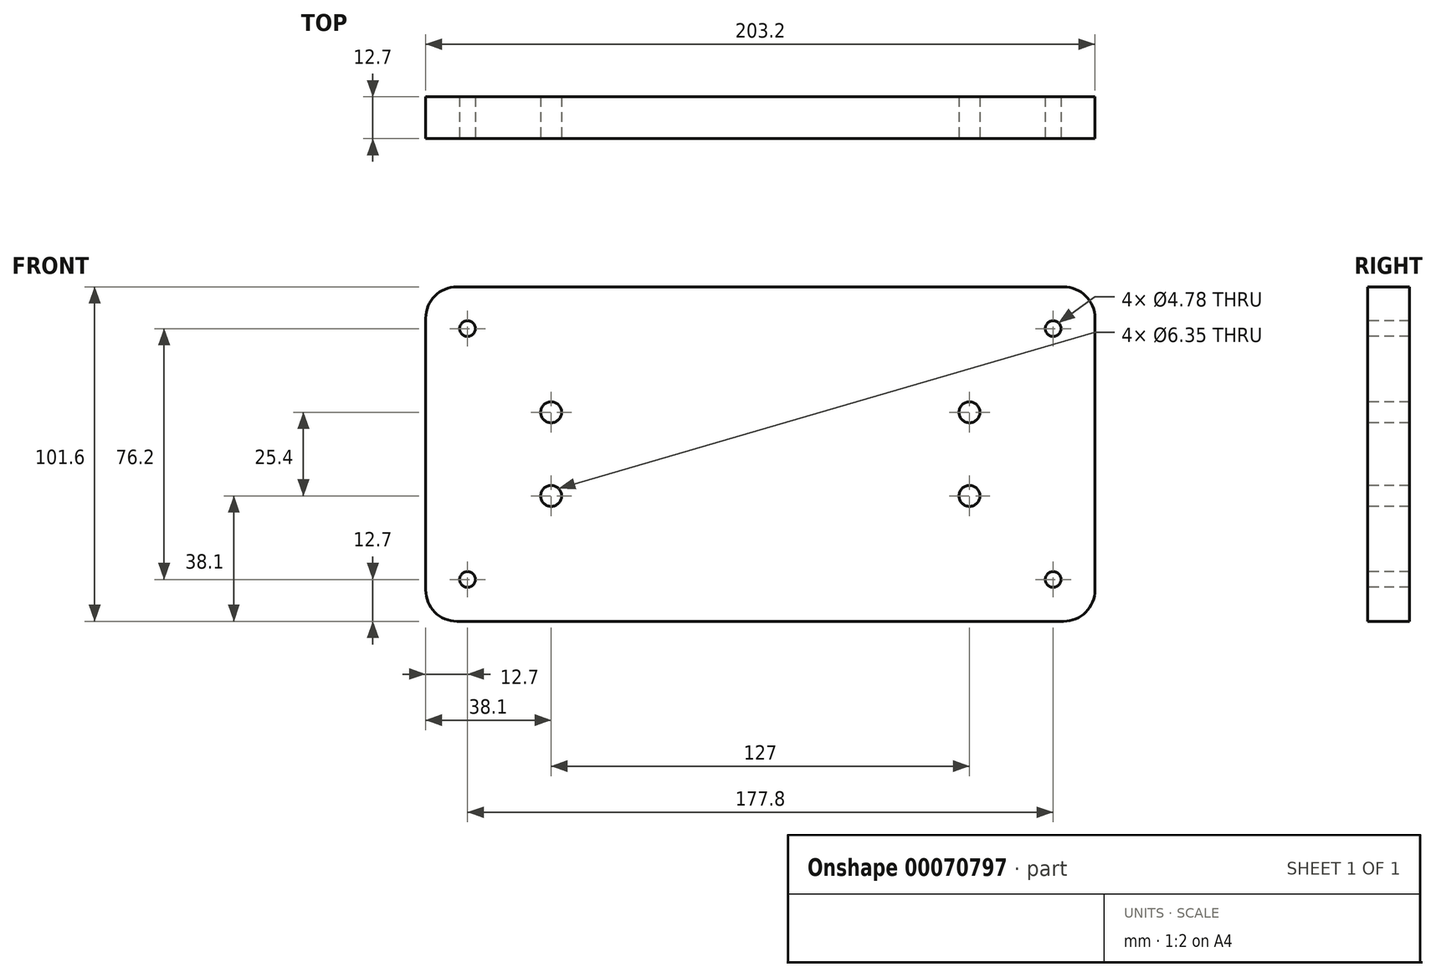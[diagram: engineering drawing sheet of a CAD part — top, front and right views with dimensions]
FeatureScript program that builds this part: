
annotation { "Feature Type Name" : "Feature", "Feature Type Description" : "" }
export const myFeature = defineFeature(function(context is Context, id is Id, definition is map)
    precondition{}
    {
        {
            var Q0;
            Q0=qCreatedBy(makeId("Front.planeOp"),FACE);
            var sketch = newSketch(context, id + "F0", { "sketchPlane" : qUnion([Q0])});
            skLineSegment(sketch, "E0.bottom", {"start": v(0, 0) * mm, "end": v(-203.2, 0) * mm});
            skLineSegment(sketch, "E0.top", {"start": v(0, 101.6) * mm, "end": v(-203.2, 101.6) * mm});
            skLineSegment(sketch, "E0.left", {"start": v(0, 0) * mm, "end": v(0, 101.6) * mm});
            skLineSegment(sketch, "E0.right", {"start": v(-203.2, 0) * mm, "end": v(-203.2, 101.6) * mm});
            skPoint(sketch, "E1", {"position": v(-190.5, 88.9) * mm});
            skPoint(sketch, "E2", {"position": v(-190.5, 12.7) * mm});
            skPoint(sketch, "E3", {"position": v(-12.7, 12.7) * mm});
            skPoint(sketch, "E4", {"position": v(-12.7, 88.9) * mm});
            skPoint(sketch, "E5", {"position": v(-131.26, 50.07) * mm});
            skPoint(sketch, "E6", {"position": v(-131.26, 29.7) * mm});
            skPoint(sketch, "E7", {"position": v(-52.98, 29.4) * mm});
            skPoint(sketch, "E8", {"position": v(-58.44, 52.7) * mm});
            skSolve(sketch);
        }
        {
            var Q0;
            Q0=makeQuery(id+"F0.imprint","IMPRINT",FACE,{"disambiguationData":[TD([[makeQuery(id+"F0.imprint","IMPRINT",EDGE,{"derivedFrom":sQuery(id+"F0.wireOp",EDGE,"E0.bottom")}),-1.0]])]});
            extrude(context, id + "F1", {"entities" : qUnion([Q0]), "depth" : 12.7 * mm});
        }
        {
            var Q0;
            Q0=makeQuery(id+"F1.opExtrude","SWEPT_EDGE",EDGE,{"disambiguationData":[OSD([sQuery(id+"F0.wireOp",EDGE,"E0.top"),sQuery(id+"F0.wireOp",EDGE,"E0.right")])]});
            var Q1;
            Q1=makeQuery(id+"F1.opExtrude","SWEPT_EDGE",EDGE,{"disambiguationData":[OSD([sQuery(id+"F0.wireOp",EDGE,"E0.bottom"),sQuery(id+"F0.wireOp",EDGE,"E0.right")])]});
            var Q2;
            Q2=makeQuery(id+"F1.opExtrude","SWEPT_EDGE",EDGE,{"disambiguationData":[OSD([sQuery(id+"F0.wireOp",EDGE,"E0.top"),sQuery(id+"F0.wireOp",EDGE,"E0.left")])]});
            var Q3;
            Q3=makeQuery(id+"F1.opExtrude","SWEPT_EDGE",EDGE,{"disambiguationData":[OSD([sQuery(id+"F0.wireOp",EDGE,"E0.bottom"),sQuery(id+"F0.wireOp",EDGE,"E0.left")])]});
            fillet(context, id + "F2", {"entities" : qUnion([Q0, Q1, Q2, Q3]), "radius" : 9.52 * mm, "tangentPropagation" : true, "allowEdgeOverflow" : false});
        }
        {
            var Q0;
            Q0=makeQuery(id+"F1.opExtrude","CAP_FACE",FACE,{"disambiguationData":[OSD([sQuery(id+"F0.wireOp",EDGE,"E0.bottom"),sQuery(id+"F0.wireOp",EDGE,"E0.top"),sQuery(id+"F0.wireOp",EDGE,"E0.left"),sQuery(id+"F0.wireOp",EDGE,"E0.right")])],"isStart":false});
            var sketch = newSketch(context, id + "F3", { "sketchPlane" : qUnion([Q0])});
            skPoint(sketch, "E9", {"position": v(-190.5, 88.9) * mm});
            skPoint(sketch, "E10", {"position": v(-190.5, 12.7) * mm});
            skPoint(sketch, "E11", {"position": v(-12.7, 12.7) * mm});
            skPoint(sketch, "E12", {"position": v(-12.7, 88.9) * mm});
            skSolve(sketch);
        }
        {
            var Q0;
            Q0=sQuery(id+"F3.wireOp",VERTEX,"E9");
            var Q1;
            Q1=sQuery(id+"F3.wireOp",VERTEX,"E10");
            var Q2;
            Q2=sQuery(id+"F3.wireOp",VERTEX,"E11");
            var Q3;
            Q3=sQuery(id+"F3.wireOp",VERTEX,"E12");
            var Q4;
            Q4=makeQuery(id+"F1.opExtrude","SWEPT_BODY",BODY,{"disambiguationData":[OSD([sQuery(id+"F0.wireOp",EDGE,"E0.bottom"),sQuery(id+"F0.wireOp",EDGE,"E0.top"),sQuery(id+"F0.wireOp",EDGE,"E0.left"),sQuery(id+"F0.wireOp",EDGE,"E0.right")])]});
            hole(context, id + "F4", {"style" : HoleStyle.SIMPLE, "holeDiameter" : 4.78 * mm, "endStyle" : HoleEndStyle.THROUGH, "locations" : qUnion([Q0, Q1, Q2, Q3]), "scope" : qUnion([Q4])});
        }
        {
            var Q0;
            Q0=makeQuery(id+"F1.opExtrude","CAP_FACE",FACE,{"disambiguationData":[OSD([sQuery(id+"F0.wireOp",EDGE,"E0.bottom"),sQuery(id+"F0.wireOp",EDGE,"E0.top"),sQuery(id+"F0.wireOp",EDGE,"E0.left"),sQuery(id+"F0.wireOp",EDGE,"E0.right")])],"isStart":false});
            var sketch = newSketch(context, id + "F5", { "sketchPlane" : qUnion([Q0])});
            skPoint(sketch, "E13", {"position": v(-165.1, 63.5) * mm});
            skPoint(sketch, "E14", {"position": v(-165.1, 38.1) * mm});
            skPoint(sketch, "E15", {"position": v(-38.1, 38.1) * mm});
            skPoint(sketch, "E16", {"position": v(-38.1, 63.5) * mm});
            skSolve(sketch);
        }
        {
            var Q0;
            Q0=sQuery(id+"F5.wireOp",VERTEX,"E13");
            var Q1;
            Q1=sQuery(id+"F5.wireOp",VERTEX,"E14");
            var Q2;
            Q2=sQuery(id+"F5.wireOp",VERTEX,"E15");
            var Q3;
            Q3=sQuery(id+"F5.wireOp",VERTEX,"E16");
            var Q4;
            Q4=makeQuery(id+"F1.opExtrude","SWEPT_BODY",BODY,{"disambiguationData":[OSD([sQuery(id+"F0.wireOp",EDGE,"E0.bottom"),sQuery(id+"F0.wireOp",EDGE,"E0.top"),sQuery(id+"F0.wireOp",EDGE,"E0.left"),sQuery(id+"F0.wireOp",EDGE,"E0.right")])]});
            hole(context, id + "F6", {"style" : HoleStyle.SIMPLE, "holeDiameter" : 6.35 * mm, "endStyle" : HoleEndStyle.THROUGH, "locations" : qUnion([Q0, Q1, Q2, Q3]), "scope" : qUnion([Q4])});
        }
    });
